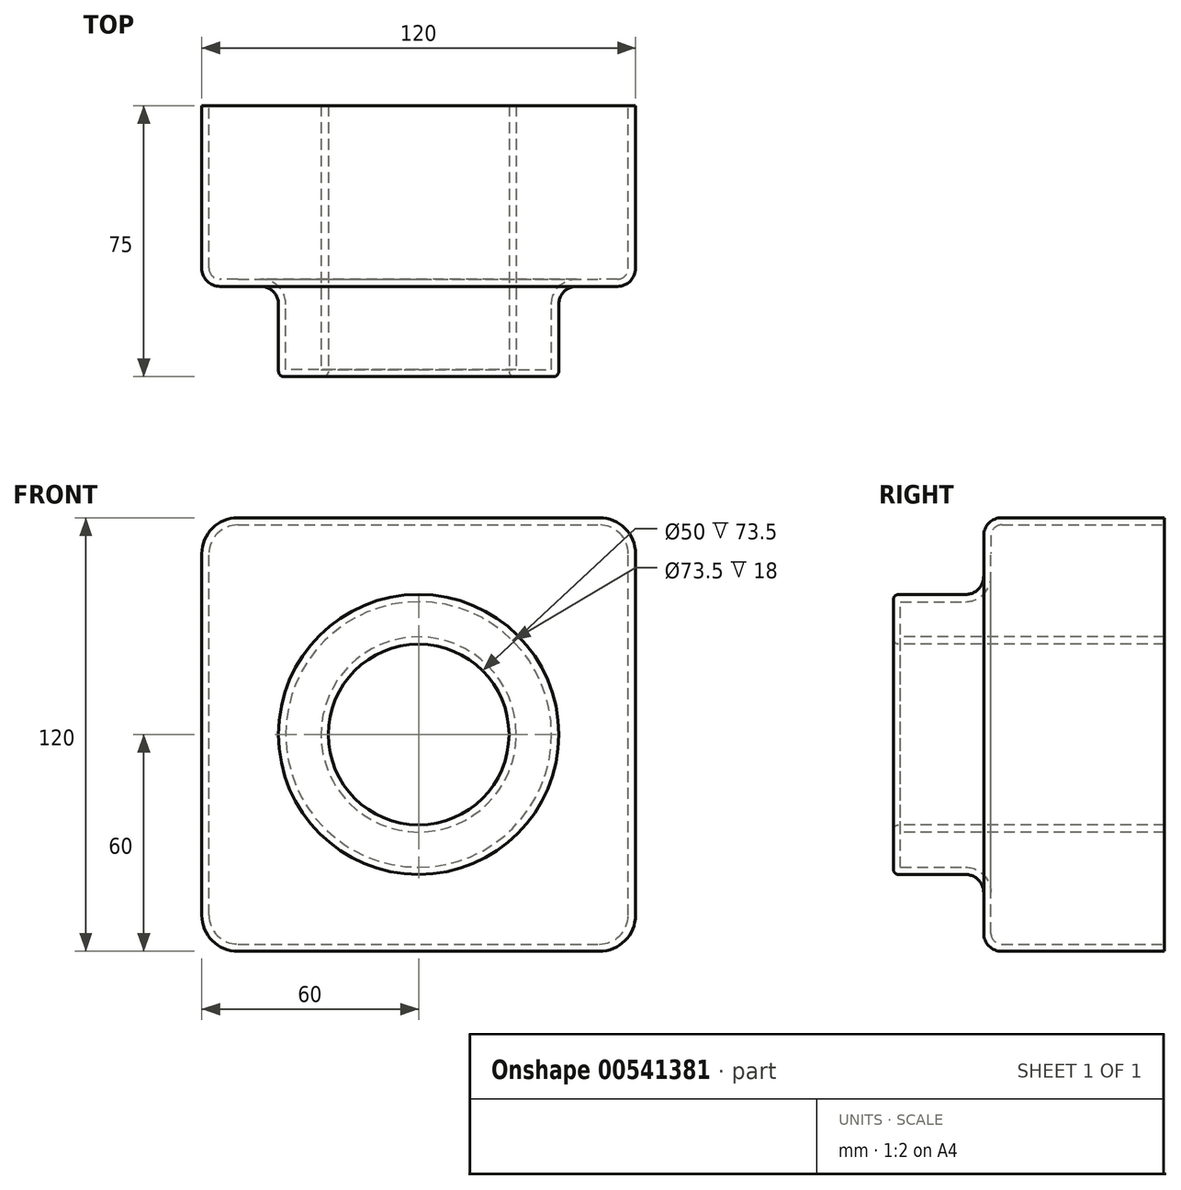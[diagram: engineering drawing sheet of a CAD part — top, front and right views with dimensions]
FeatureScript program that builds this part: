
annotation { "Feature Type Name" : "Feature", "Feature Type Description" : "" }
export const myFeature = defineFeature(function(context is Context, id is Id, definition is map)
    precondition{}
    {
        {
            var Q0;
            Q0=qCreatedBy(makeId("Front.planeOp"),FACE);
            var sketch = newSketch(context, id + "F0", { "sketchPlane" : qUnion([Q0])});
            skLineSegment(sketch, "E0.bottom", {"start": v(0, 0) * mm, "end": v(120, 0) * mm});
            skLineSegment(sketch, "E0.top", {"start": v(0, 120) * mm, "end": v(120, 120) * mm});
            skLineSegment(sketch, "E0.left", {"start": v(0, 0) * mm, "end": v(0, 120) * mm});
            skLineSegment(sketch, "E0.right", {"start": v(120, 0) * mm, "end": v(120, 120) * mm});
            skSolve(sketch);
        }
        {
            var Q0;
            Q0=makeQuery(id+"F0.imprint","IMPRINT",FACE,{"disambiguationData":[TD([[makeQuery(id+"F0.imprint","IMPRINT",EDGE,{"derivedFrom":sQuery(id+"F0.wireOp",EDGE,"E0.bottom")}),1.0]])]});
            extrude(context, id + "F1", {"entities" : qUnion([Q0]), "depth" : 50 * mm, "offsetDistance" : 25.4 * mm});
        }
        {
            var Q0;
            Q0=makeQuery(id+"F1.opExtrude","CAP_FACE",FACE,{"disambiguationData":[OSD([sQuery(id+"F0.wireOp",EDGE,"E0.bottom"),sQuery(id+"F0.wireOp",EDGE,"E0.top"),sQuery(id+"F0.wireOp",EDGE,"E0.left"),sQuery(id+"F0.wireOp",EDGE,"E0.right")])],"isStart":false});
            var sketch = newSketch(context, id + "F2", { "sketchPlane" : qUnion([Q0])});
            skCircle(sketch, "E1", {"center": v(60, 60) * mm, "radius": 38.75 * mm});
            skSolve(sketch);
        }
        {
            var Q0;
            Q0=makeQuery(id+"F2.imprint","IMPRINT",FACE,{"disambiguationData":[TD([[makeQuery(id+"F2.imprint","IMPRINT",EDGE,{"derivedFrom":sQuery(id+"F2.wireOp",EDGE,"E1")}),1.0]])]});
            extrude(context, id + "F3", {"entities" : qUnion([Q0]), "operationType" : NewBodyOperationType.ADD, "depth" : 25 * mm, "offsetDistance" : 25.4 * mm});
        }
        {
            var Q0;
            Q0=makeQuery(id+"F3.opExtrude","CAP_FACE",FACE,{"disambiguationData":[OSD([sQuery(id+"F2.wireOp",EDGE,"E1")])],"isStart":false});
            var sketch = newSketch(context, id + "F4", { "sketchPlane" : qUnion([Q0])});
            skCircle(sketch, "E2", {"center": v(60, 60) * mm, "radius": 25 * mm});
            skSolve(sketch);
        }
        {
            var Q0;
            Q0=makeQuery(id+"F4.imprint","IMPRINT",FACE,{"disambiguationData":[TD([[makeQuery(id+"F4.imprint","IMPRINT",EDGE,{"derivedFrom":sQuery(id+"F4.wireOp",EDGE,"E2")}),1.0]])]});
            extrude(context, id + "F5", {"entities" : qUnion([Q0]), "operationType" : NewBodyOperationType.REMOVE, "endBound" : BoundingType.THROUGH_ALL, "oppositeDirection" : true, "depth" : 25.4 * mm, "offsetDistance" : 25.4 * mm});
        }
        {
            var Q0;
            Q0=makeQuery(id+"F1.opExtrude","SWEPT_EDGE",EDGE,{"disambiguationData":[OSD([sQuery(id+"F0.wireOp",EDGE,"E0.bottom"),sQuery(id+"F0.wireOp",EDGE,"E0.right")])]});
            var Q1;
            Q1=makeQuery(id+"F1.opExtrude","SWEPT_EDGE",EDGE,{"disambiguationData":[OSD([sQuery(id+"F0.wireOp",EDGE,"E0.bottom"),sQuery(id+"F0.wireOp",EDGE,"E0.left")])]});
            var Q2;
            Q2=makeQuery(id+"F1.opExtrude","SWEPT_EDGE",EDGE,{"disambiguationData":[OSD([sQuery(id+"F0.wireOp",EDGE,"E0.top"),sQuery(id+"F0.wireOp",EDGE,"E0.left")])]});
            var Q3;
            Q3=makeQuery(id+"F1.opExtrude","SWEPT_EDGE",EDGE,{"disambiguationData":[OSD([sQuery(id+"F0.wireOp",EDGE,"E0.top"),sQuery(id+"F0.wireOp",EDGE,"E0.right")])]});
            fillet(context, id + "F6", {"entities" : qUnion([Q0, Q1, Q2, Q3]), "radius" : 10 * mm, "tangentPropagation" : true, "allowEdgeOverflow" : false});
        }
        {
            var Q0;
            Q0=makeQuery(id+"F3.opExtrude","CAP_FACE",FACE,{"disambiguationData":[OSD([sQuery(id+"F2.wireOp",EDGE,"E1")])],"isStart":false});
            fillet(context, id + "F7", {"entities" : qUnion([Q0]), "radius" : 1.5 * mm, "tangentPropagation" : true, "allowEdgeOverflow" : false});
        }
        {
            var Q0;
            Q0=makeQuery(id+"F1.opExtrude","CAP_FACE",FACE,{"disambiguationData":[OSD([sQuery(id+"F0.wireOp",EDGE,"E0.bottom"),sQuery(id+"F0.wireOp",EDGE,"E0.top"),sQuery(id+"F0.wireOp",EDGE,"E0.left"),sQuery(id+"F0.wireOp",EDGE,"E0.right")])],"isStart":false});
            fillet(context, id + "F8", {"entities" : qUnion([Q0]), "radius" : 5 * mm, "tangentPropagation" : true, "allowEdgeOverflow" : false});
        }
        {
            var Q0;
            Q0=makeQuery(id+"F1.opExtrude","CAP_FACE",FACE,{"disambiguationData":[OSD([sQuery(id+"F0.wireOp",EDGE,"E0.bottom"),sQuery(id+"F0.wireOp",EDGE,"E0.top"),sQuery(id+"F0.wireOp",EDGE,"E0.left"),sQuery(id+"F0.wireOp",EDGE,"E0.right")])],"isStart":true});
            shell(context, id + "F9", {"entities" : qUnion([Q0]), "thickness" : 2 * mm});
        }
    });
